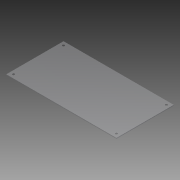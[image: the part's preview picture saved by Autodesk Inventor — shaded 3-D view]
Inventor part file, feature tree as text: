
AUTODESK INVENTOR PART (.ipt)
format: ipt  version: 2015 (Build 190159000, 159)  size: 126,464 bytes
history: native  units: mm
features: sketch x3, extrude x2, projected_geometry x2, hole x1
ambient origin geometry x8: Origin, YZ Plane, XZ Plane, XY Plane, X Axis, Y Axis, Z Axis, Center Point
bodies: Solid1 (feature_tree)
feature tree (8):
  extrude  "Extrusion1"  Depth=75.9mm
  hole  "Hole1"  [1 undecoded]
  extrude  "Extrusion2"  TaperAngle=0.0deg  [1 undecoded]
  sketch  "Sketch1"  dims[d0=145.9mm d1=75.9mm]
  sketch  "Sketch2"  dims[d2=1.0mm d3=0.0mm d4=4.85mm]
  projected_geometry  "Projected Loop1"
  sketch  "Sketch3"  dims[d5=3.0mm d6=6.0mm d7=4.0mm d8=2.0mm d9=90.0deg d10=8.0mm d11=20.594885mm d12=0.0mm d13=0.0mm d14=0.0mm d15=0.0mm d16=0.0mm d17=0.0mm d18=0.0mm d19=0.0mm d20=68.15mm d21=9.45mm d23=19.0mm d24=19.0mm d25=19.0mm d26=15.0mm d27=15.0mm d28=15.0mm d29=15.0mm d30=0.001mm d31=0.0mm]
  projected_geometry  "Projected Loop2"
note: 2 required parameter values undecoded (feature->parameter linkage not recoverable at this tier; creation-order binding heuristic only, values carry confidence <= 0.55)
